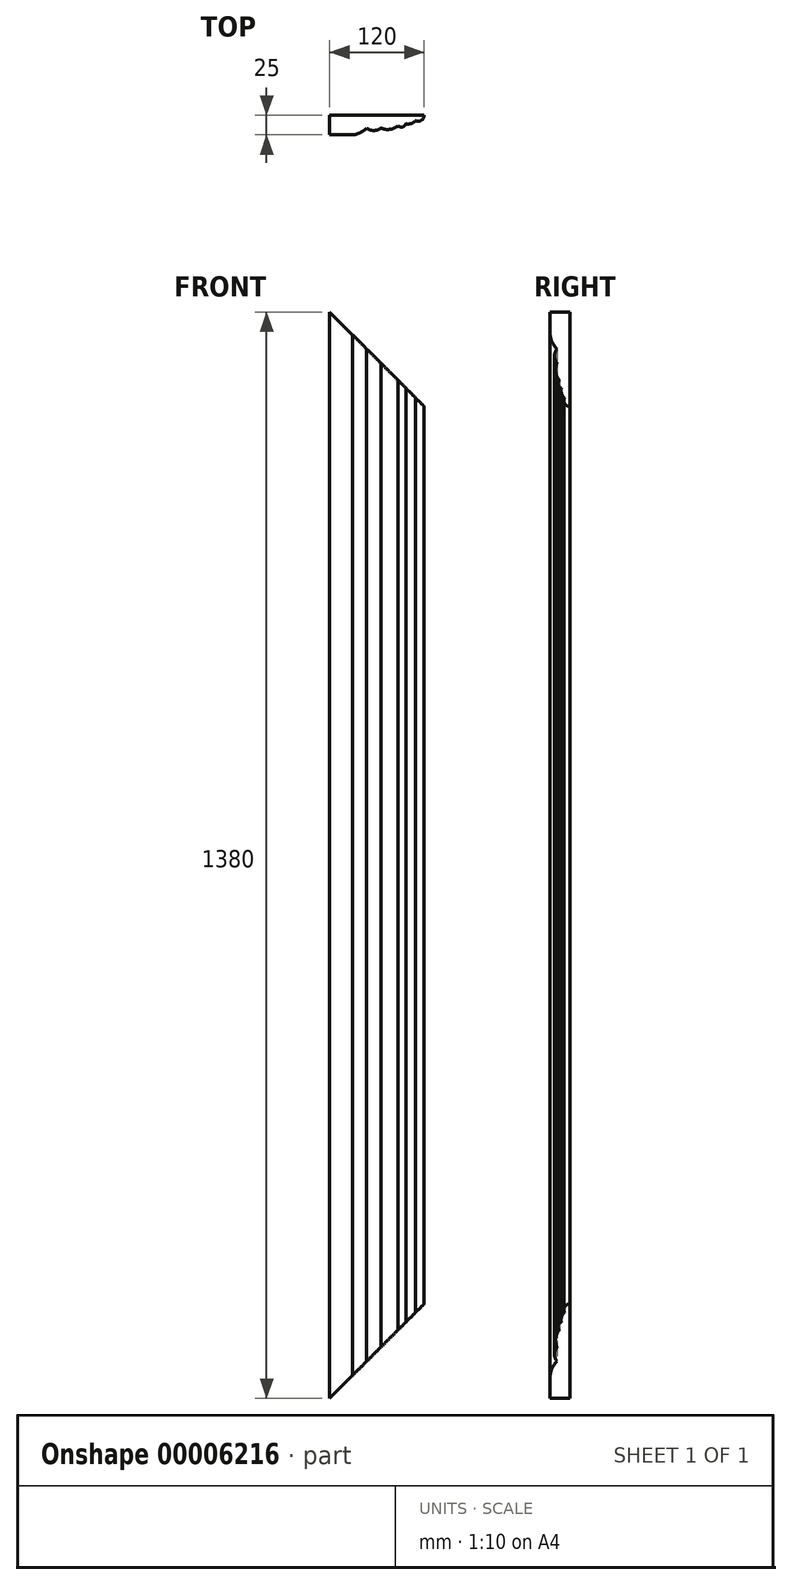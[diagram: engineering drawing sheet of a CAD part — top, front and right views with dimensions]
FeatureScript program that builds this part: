
annotation { "Feature Type Name" : "Feature", "Feature Type Description" : "" }
export const myFeature = defineFeature(function(context is Context, id is Id, definition is map)
    precondition{}
    {
        {
            var Q0;
            Q0=qCreatedBy(makeId("Top.planeOp"),FACE);
            var sketch = newSketch(context, id + "F0", { "sketchPlane" : qUnion([Q0])});
            skLineSegment(sketch, "E0.bottom", {"start": v(0, 0) * mm, "end": v(120, 0) * mm});
            skLineSegment(sketch, "E0.top", {"start": v(0, -25) * mm, "end": v(29.17, -25) * mm});
            skLineSegment(sketch, "E0.left", {"start": v(0, 0) * mm, "end": v(0, -25) * mm});
            skArc(sketch, "E1", {"start": v(29.17, -25) * mm, "mid": v(38.77, -22.24) * mm, "end": v(46.87, -16.4) * mm});
            skArc(sketch, "E2", {"start": v(46.87, -16.4) * mm, "mid": v(55.83, -19.44) * mm, "end": v(64.79, -16.4) * mm});
            skArc(sketch, "E3", {"start": v(64.79, -16.4) * mm, "mid": v(76.31, -17.94) * mm, "end": v(86.98, -13.34) * mm});
            skArc(sketch, "E4", {"start": v(86.98, -13.34) * mm, "mid": v(92.5, -14.89) * mm, "end": v(96.58, -10.84) * mm});
            skArc(sketch, "E5", {"start": v(96.58, -10.84) * mm, "mid": v(103.41, -10.57) * mm, "end": v(109.18, -6.9) * mm});
            skArc(sketch, "E6", {"start": v(109.18, -6.9) * mm, "mid": v(116.48, -6.42) * mm, "end": v(120, 0) * mm});
            skSolve(sketch);
        }
        {
            var Q0;
            Q0=makeQuery(id+"F0.imprint","IMPRINT",FACE,{"disambiguationData":[TD([[makeQuery(id+"F0.imprint","IMPRINT",EDGE,{"derivedFrom":sQuery(id+"F0.wireOp",EDGE,"E0.bottom")}),-1.0]])]});
            extrude(context, id + "F1", {"entities" : qUnion([Q0]), "depth" : 1380 * mm});
        }
        {
            var Q0;
            Q0=makeQuery(id+"F1.opExtrude","SWEPT_FACE",FACE,{"disambiguationData":[OSD([sQuery(id+"F0.wireOp",EDGE,"E0.bottom")])]});
            var sketch = newSketch(context, id + "F2", { "sketchPlane" : qUnion([Q0])});
            skLineSegment(sketch, "E7", {"start": v(0, 0) * mm, "end": v(-120, 120) * mm});
            skLineSegment(sketch, "E8", {"start": v(0, 1380) * mm, "end": v(-120, 1260) * mm});
            skLineSegment(sketch, "E9", {"start": v(-120, 120) * mm, "end": v(-120, 0) * mm});
            skLineSegment(sketch, "E10", {"start": v(-120, 0) * mm, "end": v(0, 0) * mm});
            skLineSegment(sketch, "E11", {"start": v(0, 1380) * mm, "end": v(-120, 1380) * mm});
            skLineSegment(sketch, "E12", {"start": v(-120, 1380) * mm, "end": v(-120, 1260) * mm});
            skSolve(sketch);
        }
        {
            var Q0;
            Q0=qSketchRegion(id+"F2",true);
            extrude(context, id + "F3", {"entities" : qUnion([Q0]), "operationType" : NewBodyOperationType.REMOVE, "oppositeDirection" : true, "depth" : 25 * mm});
        }
    });
